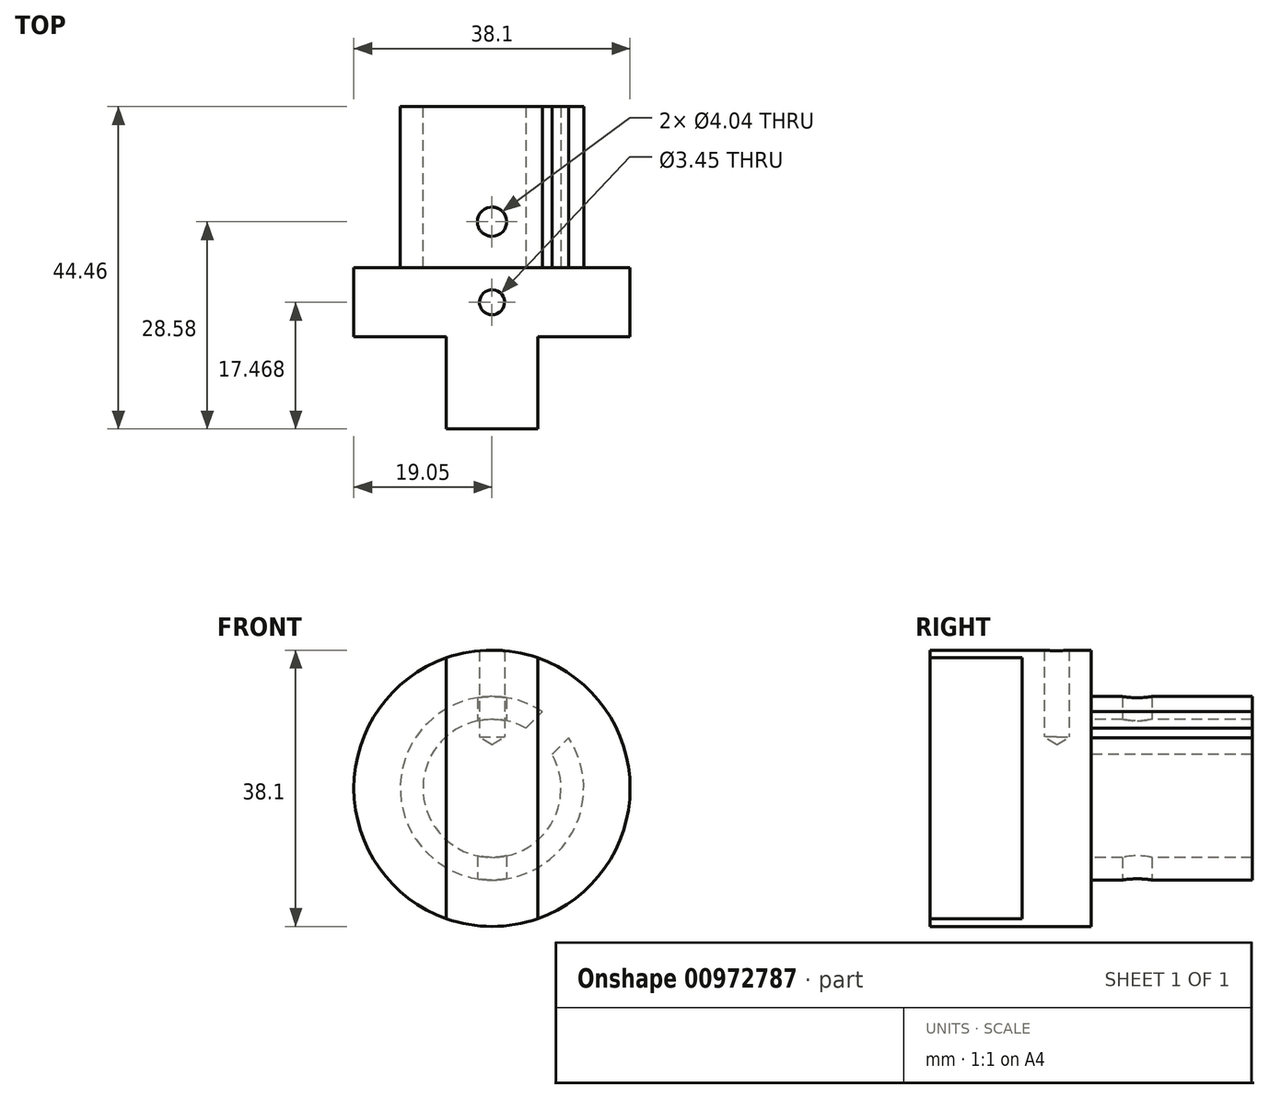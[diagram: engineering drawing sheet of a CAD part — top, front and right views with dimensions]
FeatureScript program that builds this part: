
annotation { "Feature Type Name" : "Feature", "Feature Type Description" : "" }
export const myFeature = defineFeature(function(context is Context, id is Id, definition is map)
    precondition{}
    {
        {
            var Q0;
            Q0=qCreatedBy(makeId("Front.planeOp"),FACE);
            var sketch = newSketch(context, id + "F0", { "sketchPlane" : qUnion([Q0])});
            skCircle(sketch, "E0", {"center": v(0, 0) * mm, "radius": 12.65 * mm});
            skCircle(sketch, "E1", {"center": v(0, 0) * mm, "radius": 9.53 * mm});
            skSolve(sketch);
        }
        {
            var Q0;
            Q0=makeQuery(id+"F0.imprint","IMPRINT",FACE,{"disambiguationData":[TD([[makeQuery(id+"F0.imprint","IMPRINT",EDGE,{"derivedFrom":sQuery(id+"F0.wireOp",EDGE,"E0")}),1.0]])]});
            extrude(context, id + "F1", {"entities" : qUnion([Q0]), "oppositeDirection" : true, "depth" : 22.22 * mm, "offsetDistance" : 25.4 * mm});
        }
        {
            var Q0;
            Q0=makeQuery(id+"F1.opExtrude","CAP_FACE",FACE,{"disambiguationData":[OSD([sQuery(id+"F0.wireOp",EDGE,"E0"),sQuery(id+"F0.wireOp",EDGE,"E1")])],"isStart":true});
            var sketch = newSketch(context, id + "F2", { "sketchPlane" : qUnion([Q0])});
            skCircle(sketch, "E2", {"center": v(0, 0) * mm, "radius": 19.05 * mm});
            skSolve(sketch);
        }
        {
            var Q0;
            Q0=makeQuery(id+"F2.imprint","IMPRINT",FACE,{"disambiguationData":[TD([[makeQuery(id+"F2.imprint","IMPRINT",EDGE,{"derivedFrom":makeQuery(id+"F1.opExtrude","CAP_EDGE",EDGE,{"disambiguationData":[OSD([sQuery(id+"F0.wireOp",EDGE,"E1")])],"isStart":true})}),1.0]])]});
            var Q1;
            Q1=makeQuery(id+"F2.imprint","IMPRINT",FACE,{"disambiguationData":[TD([[makeQuery(id+"F2.imprint","IMPRINT",EDGE,{"derivedFrom":makeQuery(id+"F1.opExtrude","CAP_EDGE",EDGE,{"disambiguationData":[OSD([sQuery(id+"F0.wireOp",EDGE,"E0")])],"isStart":true})}),1.0]])]});
            var Q2;
            Q2=makeQuery(id+"F2.imprint","IMPRINT",FACE,{"disambiguationData":[TD([[makeQuery(id+"F2.imprint","IMPRINT",EDGE,{"derivedFrom":sQuery(id+"F2.wireOp",EDGE,"E2")}),1.0]])]});
            extrude(context, id + "F3", {"entities" : qUnion([Q0, Q1, Q2]), "operationType" : NewBodyOperationType.ADD, "depth" : 9.52 * mm, "offsetDistance" : 25.4 * mm});
        }
        {
            var Q0;
            Q0=makeQuery(id+"F3.opExtrude","CAP_FACE",FACE,{"disambiguationData":[OSD([sQuery(id+"F2.wireOp",EDGE,"E2")])],"isStart":false});
            var sketch = newSketch(context, id + "F4", { "sketchPlane" : qUnion([Q0])});
            skCircle(sketch, "E3", {"center": v(0, 0) * mm, "radius": 19.05 * mm, "construction": true});
            skLineSegment(sketch, "E4.0", {"start": v(-6.3, 17.98) * mm, "end": v(-6.3, -17.98) * mm});
            skLineSegment(sketch, "E5.0", {"start": v(6.3, 17.98) * mm, "end": v(6.3, -17.98) * mm});
            skSolve(sketch);
        }
        {
            var Q0;
            {var subQ0=sQuery(id+"F4.wireOp",EDGE,"E4.0");Q0=makeQuery(id+"F4.imprint","IMPRINT",FACE,{"disambiguationData":[TD([[makeQuery(id+"F4.imprint","IMPRINT",EDGE,{"derivedFrom":subQ0}),1.0]])]});}
            extrude(context, id + "F5", {"entities" : qUnion([Q0]), "operationType" : NewBodyOperationType.ADD, "depth" : 12.7 * mm, "offsetDistance" : 25.4 * mm});
        }
        {
            var Q0;
            Q0=qCreatedBy(makeId("Top.planeOp"),FACE);
            cPlane(context, id + "F6", {"entities" : qUnion([Q0]), "cplaneType" : CPlaneType.OFFSET, "offset" : 19.05 * mm, "width" : 152.4 * mm, "height" : 152.4 * mm});
        }
        {
            var Q0;
            Q0=qCreatedBy(id+"F6.planeOp",FACE);
            var sketch = newSketch(context, id + "F7", { "sketchPlane" : qUnion([Q0])});
            skPoint(sketch, "E6", {"position": v(0, 6.35) * mm});
            skPoint(sketch, "E7", {"position": v(0, -4.76) * mm});
            skSolve(sketch);
        }
        {
            var Q0;
            Q0=sQuery(id+"F7.wireOp",VERTEX,"E6");
            var Q1;
            Q1=makeQuery(id+"F1.opExtrude","SWEPT_BODY",BODY,{"disambiguationData":[OSD([sQuery(id+"F0.wireOp",EDGE,"E0"),sQuery(id+"F0.wireOp",EDGE,"E1")])]});
            hole(context, id + "F8", {"style" : HoleStyle.SIMPLE, "endStyle" : HoleEndStyle.THROUGH, "standardTappedOrClearance" : lookupTablePath({ "standard" : "ANSI", "engagement" : "75%", "pitch" : "32 tpi", "size" : "#10", "type" : "Tapped" }), "standardBlindInLast" : lookupTablePath({ "standard" : "ANSI", "fit" : "Normal", "engagement" : "75%", "pitch" : "32 tpi", "size" : "#10", "type" : "Clearance & tapped" }), "holeDiameter" : 4.04 * mm, "majorDiameter" : 4.83 * mm, "showTappedDepth" : true, "isTappedThrough" : true, "tappedDepth" : 9.52 * mm, "tapClearance" : 3, "locations" : qUnion([Q0]), "scope" : qUnion([Q1]), "startStyle" : HoleStartStyle.PART});
        }
        {
            var Q0;
            Q0=makeQuery(id+"F1.opExtrude","SWEPT_FACE",FACE,{"disambiguationData":[OSD([sQuery(id+"F0.wireOp",EDGE,"E0")])]});
            var Q1;
            Q1=qCreatedBy(makeId("Right.planeOp"),FACE);
            cPlane(context, id + "F9", {"entities" : qUnion([Q0, Q1]), "cplaneType" : CPlaneType.LINE_ANGLE, "offset" : 12.57 * mm, "angle" : 45 * degree, "width" : 152.4 * mm, "height" : 152.4 * mm});
        }
        {
            var Q0;
            Q0=qCreatedBy(id+"F9.planeOp",FACE);
            cPlane(context, id + "F10", {"entities" : qUnion([Q0]), "cplaneType" : CPlaneType.OFFSET, "offset" : 12.65 * mm, "oppositeDirection" : true, "width" : 152.4 * mm, "height" : 152.4 * mm});
        }
        {
            var Q0;
            Q0=qCreatedBy(id+"F10.planeOp",FACE);
            var sketch = newSketch(context, id + "F11", { "sketchPlane" : qUnion([Q0])});
            skLineSegment(sketch, "E8.0", {"start": v(0, 2.54) * mm, "end": v(-22.23, 2.54) * mm});
            skLineSegment(sketch, "E9.0", {"start": v(0, -2.54) * mm, "end": v(-22.23, -2.54) * mm});
            skLineSegment(sketch, "E10", {"start": v(0, -2.54) * mm, "end": v(0, 2.54) * mm});
            skLineSegment(sketch, "E11", {"start": v(-22.23, 2.54) * mm, "end": v(-22.23, -2.54) * mm});
            skSolve(sketch);
        }
        {
            var Q0;
            Q0=makeQuery(id+"F11.imprint","IMPRINT",FACE,{"disambiguationData":[TD([[makeQuery(id+"F11.imprint","IMPRINT",EDGE,{"derivedFrom":sQuery(id+"F11.wireOp",EDGE,"E8.0")}),1.0]])]});
            extrude(context, id + "F12", {"entities" : qUnion([Q0]), "operationType" : NewBodyOperationType.REMOVE, "depth" : 12.7 * mm, "offsetDistance" : 25.4 * mm});
        }
        {
            var Q0;
            Q0=sQuery(id+"F7.wireOp",VERTEX,"E7");
            var Q1;
            Q1=makeQuery(id+"F1.opExtrude","SWEPT_BODY",BODY,{"disambiguationData":[OSD([sQuery(id+"F0.wireOp",EDGE,"E0"),sQuery(id+"F0.wireOp",EDGE,"E1")])]});
            hole(context, id + "F13", {"style" : HoleStyle.SIMPLE, "endStyle" : HoleEndStyle.BLIND, "standardTappedOrClearance" : lookupTablePath({ "standard" : "ANSI", "engagement" : "75%", "pitch" : "32 tpi", "size" : "#8", "type" : "Tapped" }), "standardBlindInLast" : lookupTablePath({ "standard" : "ANSI", "fit" : "Normal", "engagement" : "75%", "pitch" : "32 tpi", "size" : "#8", "type" : "Clearance & tapped" }), "holeDiameter" : 3.45 * mm, "majorDiameter" : 4.17 * mm, "showTappedDepth" : true, "holeDepth" : 11.9 * mm, "tappedDepth" : 9.52 * mm, "tapClearance" : 3, "locations" : qUnion([Q0]), "scope" : qUnion([Q1]), "startStyle" : HoleStartStyle.PART});
        }
    });
